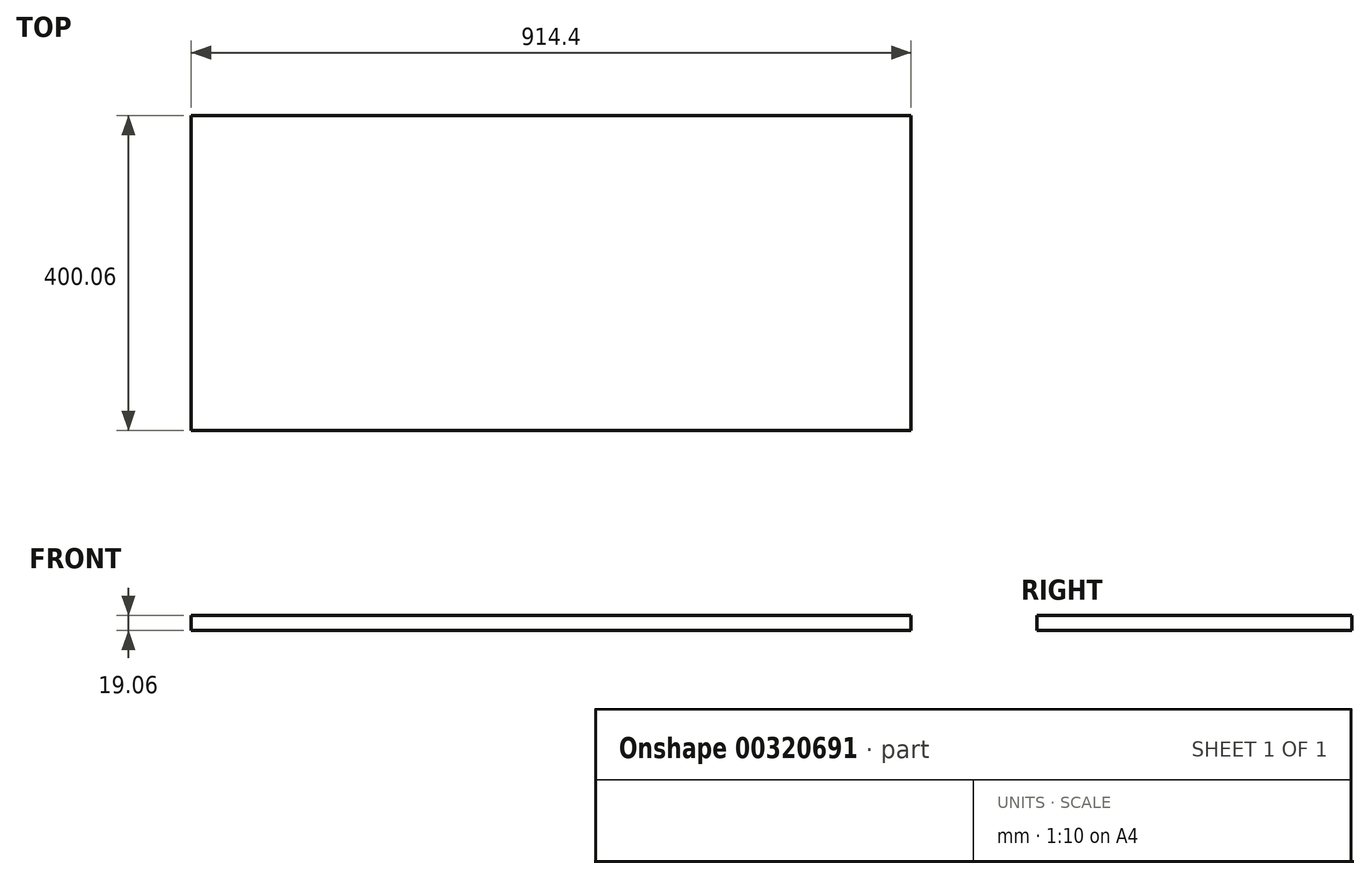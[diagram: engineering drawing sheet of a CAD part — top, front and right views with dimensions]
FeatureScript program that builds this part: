
annotation { "Feature Type Name" : "Feature", "Feature Type Description" : "" }
export const myFeature = defineFeature(function(context is Context, id is Id, definition is map)
    precondition{}
    {
        {
            var Q0;
            Q0=qCreatedBy(makeId("Front.planeOp"),FACE);
            var sketch = newSketch(context, id + "F0", { "sketchPlane" : qUnion([Q0])});
            skLineSegment(sketch, "E0.bottom", {"start": v(-457.2, -9.53) * mm, "end": v(457.2, -9.53) * mm});
            skLineSegment(sketch, "E0.top", {"start": v(-457.2, 9.53) * mm, "end": v(457.2, 9.53) * mm});
            skLineSegment(sketch, "E0.left", {"start": v(-457.2, -9.53) * mm, "end": v(-457.2, 9.53) * mm});
            skLineSegment(sketch, "E0.right", {"start": v(457.2, -9.53) * mm, "end": v(457.2, 9.53) * mm});
            skPoint(sketch, "E0.middle", {"position": v(0, 0) * mm});
            skSolve(sketch);
        }
        {
            var Q0;
            Q0=makeQuery(id+"F0.imprint","IMPRINT",FACE,{"disambiguationData":[TD([[makeQuery(id+"F0.imprint","IMPRINT",EDGE,{"derivedFrom":sQuery(id+"F0.wireOp",EDGE,"E0.bottom")}),1.0]])]});
            extrude(context, id + "F1", {"entities" : qUnion([Q0]), "depth" : 400.05 * mm, "symmetric" : true});
        }
    });
